# Revit family: Reece_Tap_Posh_Bristol MK2_Shower Mixer_Extended Lever
name_source: partatom
category: Plumbing Fixtures
revit_build: Autodesk Revit 2018 (Build: 20190510_1515(x64)
units: mm (PartAtom-declared; Revit-internal decimal feet)

## family parameters
Cut with Voids When Loaded = No
Host = Face
Part Type = Normal
Room Calculation Point = Yes
Round Connector Dimension = Use Diameter
Shared = Yes

## types (1)
- Extended Lever_Chrome
    CWFU = 0
    Default Elevation = 1000 mm  [stored 3.28084 ft]
    Description = Posh Bristol MK2 Shower Mixer Tap with Extended Lever Chrome
    Disclaimer = THIS FILE IS THE PROPERTY OF THE REECE GROUP. IT MAY NOT BE REPRODUCED, REVERSE-ENGINEERED OR MODIFIED. ANY REPUBLICATION, TRANSMISSION OR DISTRIBUTION FOR THE PURPOSE OF COMMERCIALLY EXPLOITING THE FILES IS PROHIBITED.
    HWFU = 0
    Keynote = Product #9505251, Reece_Tap_Posh_Bristol MK2_Shower Mixer_Extended Lever - Extended Lever_Chrome
    Manufacturer = Posh
    Model = Bristol MK2
    Reece_Detail_Additional = Extended Lever
    Reece_Detail_Disclaimer = THIS FILE IS THE PROPERTY OF THE REECE GROUP. IT MAY NOT BE REPRODUCED, REVERSE-ENGINEERED OR MODIFIED. ANY REPUBLICATION, TRANSMISSION OR DISTRIBUTION FOR THE PURPOSE OF COMMERCIALLY EXPLOITING THE FILES IS PROHIBITED.
    Reece_Detail_Installation = Shower Mixer
    Reece_Material-Main = Reece_Brass_Chrome
    Reece_Material_Secondary = Reece_Rubber_Black
    Reece_Overall_Diameter = 135 mm  [stored 0.442913 ft]
    Reece_Overall_Height = 160 mm  [stored 0.524934 ft]
    Reece_Overall_Projection = 292 mm  [stored 0.958005 ft]
    Reece_Product_Brand = Posh
    Reece_Product_Description = Posh Bristol MK2 Shower Mixer Tap with Extended Lever Chrome
    Reece_Product_Mount = Wall Mounted
    Reece_Product_Number = 9505251
    Reece_Product_Sub Brand = Bristol MK2
    Reece_Product_Type = Tap
    Reece_Product_Web Page = https://www.reece.com.au
    Reece_Tap_Inlet = 12 mm  [stored 0.0393701 ft]
    Type Comments = Tap
    URL = https://www.reece.com.au
    WFU = 0

note: [stored X ft] marks values corroborated as IEEE doubles in the binary element streams (Revit-internal decimal feet)

## geometry (parser evidence)
native form markers: Sweep x2
no freeform markers — native parametric forms only
